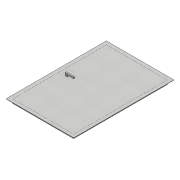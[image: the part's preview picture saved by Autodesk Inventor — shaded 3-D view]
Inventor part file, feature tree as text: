
AUTODESK INVENTOR PART (.ipt)
format: ipt  version: 2017 (Build 210142000, 142)  size: 158,208 bytes
history: native  units: mm
features: extrude x6, sketch x6, draft x1
ambient origin geometry x8: Origin, YZ Plane, XZ Plane, XY Plane, X Axis, Y Axis, Z Axis, Center Point
bodies: Solid1 (feature_tree)
feature tree (13):
  extrude  "Extrusion1"  Depth=1166.0mm
  extrude  "Extrusion2"  Depth=3.0mm
  extrude  "Extrusion3"  Depth=25.0mm
  extrude  "Extrusion4"  Depth=80.0mm
  draft  "FaceDraft2"
  extrude  "Extrusion5"  Depth=15.0mm
  extrude  "Extrusion7"  Depth=80.0mm TaperAngle=0.0deg
  sketch  "Sketch1"  dims[d0=759.6mm d1=1166.0mm]
  sketch  "Sketch2"  dims[d2=3.0mm d3=0.0mm d4=3.0mm]
  sketch  "Sketch3"  dims[d5=50.0mm d6=0.0mm d7=25.0mm]
  sketch  "Sketch4"  dims[d8=15.0mm d9=80.0mm]
  sketch  "Sketch5"  dims[d10=35.0mm d11=0.0mm d12=15.0mm]
  sketch  "Sketch7"  dims[d13=15.0mm d14=80.0mm d15=0.0mm d17=0.174533mm d18=12.5mm d19=12.0mm d20=10.0mm d21=80.0mm d22=0.0mm d26=40.0mm d27=3.0mm d28=0.0mm]
